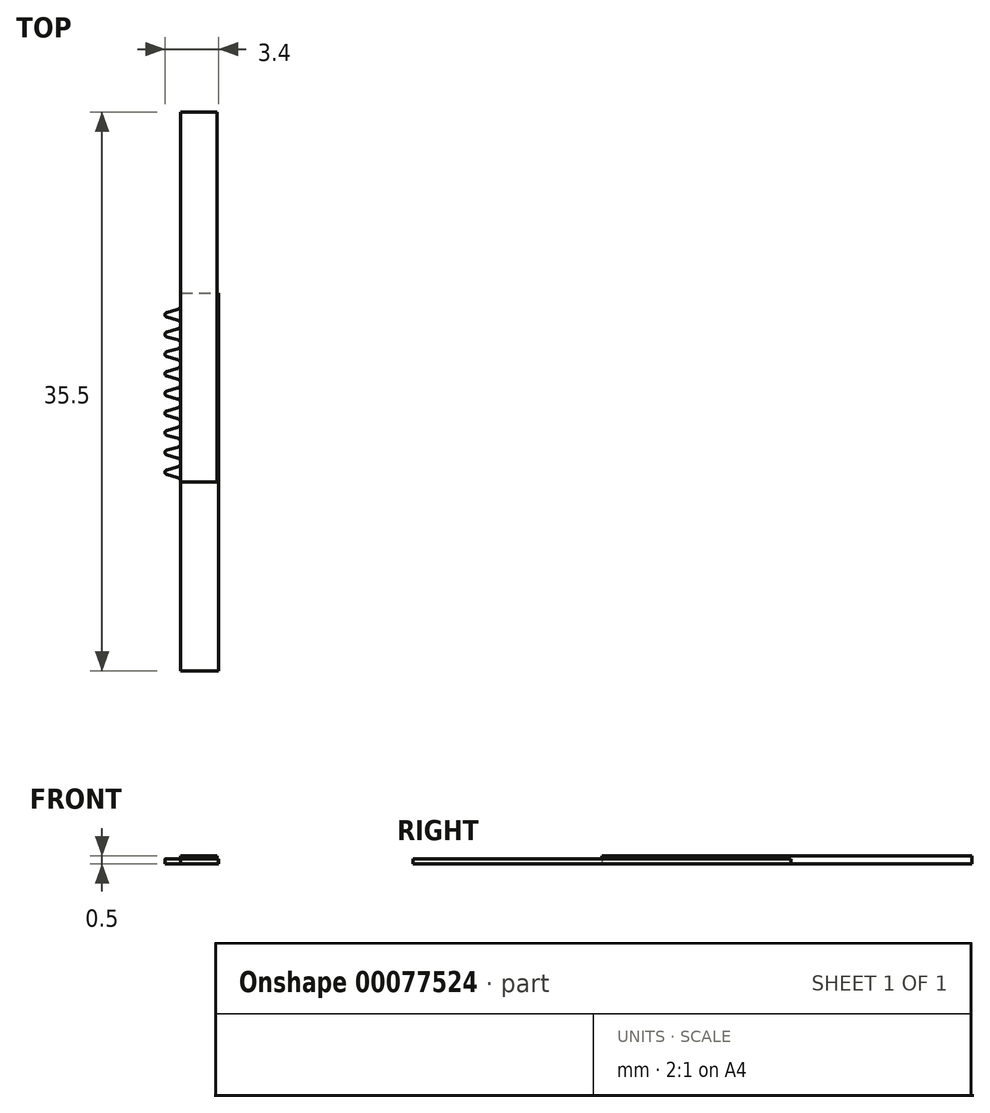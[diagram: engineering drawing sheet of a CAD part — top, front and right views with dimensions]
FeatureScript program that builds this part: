
annotation { "Feature Type Name" : "Feature", "Feature Type Description" : "" }
export const myFeature = defineFeature(function(context is Context, id is Id, definition is map)
    precondition{}
    {
        {
            var Q0;
            Q0=qCreatedBy(makeId("Top.planeOp"),FACE);
            var sketch = newSketch(context, id + "F0", { "sketchPlane" : qUnion([Q0])});
            skLineSegment(sketch, "E0.bottom", {"start": v(0, 12) * mm, "end": v(2.4, 12) * mm});
            skLineSegment(sketch, "E0.top", {"start": v(0, -12) * mm, "end": v(2.4, -12) * mm});
            skLineSegment(sketch, "E0.left", {"start": v(0, 12) * mm, "end": v(0, -12) * mm});
            skLineSegment(sketch, "E0.right", {"start": v(2.4, 12) * mm, "end": v(2.4, -12) * mm});
            skLineSegment(sketch, "E1", {"start": v(2.4, 0.63) * mm, "end": v(-1, 0.62) * mm, "construction": true});
            skLineSegment(sketch, "E2", {"start": v(2.4, 1.88) * mm, "end": v(-1, 1.87) * mm, "construction": true});
            skArc(sketch, "E3", {"start": v(-0.88, 0.78) * mm, "mid": v(-1, 0.62) * mm, "end": v(-0.88, 0.47) * mm});
            skArc(sketch, "E4", {"start": v(-0.22, 0.96) * mm, "mid": v(-0.06, 1.07) * mm, "end": v(0, 1.25) * mm});
            skPoint(sketch, "E5", {"position": v(0, 1.25) * mm});
            skLineSegment(sketch, "E6", {"start": v(-0.88, 0.78) * mm, "end": v(-0.22, 0.96) * mm});
            skArc(sketch, "E7", {"start": v(0, 0) * mm, "mid": v(-0.06, 0.18) * mm, "end": v(-0.22, 0.29) * mm});
            skLineSegment(sketch, "E8", {"start": v(-0.88, 0.47) * mm, "end": v(-0.22, 0.29) * mm});
            skArc(sketch, "E9.1.0.0", {"start": v(-0.22, 2.21) * mm, "mid": v(-0.06, 2.32) * mm, "end": v(0, 2.5) * mm});
            skLineSegment(sketch, "E9.1.0.1", {"start": v(-0.88, 2.03) * mm, "end": v(-0.22, 2.21) * mm});
            skArc(sketch, "E9.1.0.2", {"start": v(-0.88, 2.03) * mm, "mid": v(-1, 1.87) * mm, "end": v(-0.88, 1.72) * mm});
            skLineSegment(sketch, "E9.1.0.3", {"start": v(-0.88, 1.72) * mm, "end": v(-0.22, 1.54) * mm});
            skArc(sketch, "E9.1.0.4", {"start": v(0, 1.25) * mm, "mid": v(-0.06, 1.43) * mm, "end": v(-0.22, 1.54) * mm});
            skArc(sketch, "E9.2.0.0", {"start": v(-0.22, 3.46) * mm, "mid": v(-0.06, 3.57) * mm, "end": v(0, 3.75) * mm});
            skLineSegment(sketch, "E9.2.0.1", {"start": v(-0.88, 3.28) * mm, "end": v(-0.22, 3.46) * mm});
            skArc(sketch, "E9.2.0.2", {"start": v(-0.88, 3.28) * mm, "mid": v(-1, 3.12) * mm, "end": v(-0.88, 2.97) * mm});
            skLineSegment(sketch, "E9.2.0.3", {"start": v(-0.88, 2.97) * mm, "end": v(-0.22, 2.79) * mm});
            skArc(sketch, "E9.2.0.4", {"start": v(0, 2.5) * mm, "mid": v(-0.06, 2.68) * mm, "end": v(-0.22, 2.79) * mm});
            skArc(sketch, "E9.3.0.0", {"start": v(-0.22, 4.71) * mm, "mid": v(-0.06, 4.82) * mm, "end": v(0, 5) * mm});
            skLineSegment(sketch, "E9.3.0.1", {"start": v(-0.88, 4.53) * mm, "end": v(-0.22, 4.71) * mm});
            skArc(sketch, "E9.3.0.2", {"start": v(-0.88, 4.53) * mm, "mid": v(-1, 4.37) * mm, "end": v(-0.88, 4.22) * mm});
            skLineSegment(sketch, "E9.3.0.3", {"start": v(-0.88, 4.22) * mm, "end": v(-0.22, 4.04) * mm});
            skArc(sketch, "E9.3.0.4", {"start": v(0, 3.75) * mm, "mid": v(-0.06, 3.93) * mm, "end": v(-0.22, 4.04) * mm});
            skArc(sketch, "E9.4.0.0", {"start": v(-0.22, 5.96) * mm, "mid": v(-0.06, 6.07) * mm, "end": v(0, 6.25) * mm});
            skLineSegment(sketch, "E9.4.0.1", {"start": v(-0.88, 5.78) * mm, "end": v(-0.22, 5.96) * mm});
            skArc(sketch, "E9.4.0.2", {"start": v(-0.88, 5.78) * mm, "mid": v(-1, 5.62) * mm, "end": v(-0.88, 5.47) * mm});
            skLineSegment(sketch, "E9.4.0.3", {"start": v(-0.88, 5.47) * mm, "end": v(-0.22, 5.29) * mm});
            skArc(sketch, "E9.4.0.4", {"start": v(0, 5) * mm, "mid": v(-0.06, 5.18) * mm, "end": v(-0.22, 5.29) * mm});
            skArc(sketch, "E9.5.0.0", {"start": v(-0.22, 7.21) * mm, "mid": v(-0.06, 7.32) * mm, "end": v(0, 7.5) * mm});
            skLineSegment(sketch, "E9.5.0.1", {"start": v(-0.88, 7.03) * mm, "end": v(-0.22, 7.21) * mm});
            skArc(sketch, "E9.5.0.2", {"start": v(-0.88, 7.03) * mm, "mid": v(-1, 6.88) * mm, "end": v(-0.88, 6.72) * mm});
            skLineSegment(sketch, "E9.5.0.3", {"start": v(-0.88, 6.72) * mm, "end": v(-0.22, 6.54) * mm});
            skArc(sketch, "E9.5.0.4", {"start": v(0, 6.25) * mm, "mid": v(-0.06, 6.43) * mm, "end": v(-0.22, 6.54) * mm});
            skArc(sketch, "E9.6.0.0", {"start": v(-0.22, 8.46) * mm, "mid": v(-0.06, 8.57) * mm, "end": v(0, 8.75) * mm});
            skLineSegment(sketch, "E9.6.0.1", {"start": v(-0.88, 8.28) * mm, "end": v(-0.22, 8.46) * mm});
            skArc(sketch, "E9.6.0.2", {"start": v(-0.88, 8.28) * mm, "mid": v(-1, 8.12) * mm, "end": v(-0.88, 7.97) * mm});
            skLineSegment(sketch, "E9.6.0.3", {"start": v(-0.88, 7.97) * mm, "end": v(-0.22, 7.79) * mm});
            skArc(sketch, "E9.6.0.4", {"start": v(0, 7.5) * mm, "mid": v(-0.06, 7.68) * mm, "end": v(-0.22, 7.79) * mm});
            skArc(sketch, "E9.7.0.0", {"start": v(-0.22, 9.71) * mm, "mid": v(-0.06, 9.82) * mm, "end": v(0, 10) * mm});
            skLineSegment(sketch, "E9.7.0.1", {"start": v(-0.88, 9.53) * mm, "end": v(-0.22, 9.71) * mm});
            skArc(sketch, "E9.7.0.2", {"start": v(-0.88, 9.53) * mm, "mid": v(-1, 9.38) * mm, "end": v(-0.88, 9.22) * mm});
            skLineSegment(sketch, "E9.7.0.3", {"start": v(-0.88, 9.22) * mm, "end": v(-0.22, 9.04) * mm});
            skArc(sketch, "E9.7.0.4", {"start": v(0, 8.75) * mm, "mid": v(-0.06, 8.93) * mm, "end": v(-0.22, 9.04) * mm});
            skArc(sketch, "E9.8.0.0", {"start": v(-0.22, 10.96) * mm, "mid": v(-0.06, 11.07) * mm, "end": v(0, 11.25) * mm});
            skLineSegment(sketch, "E9.8.0.1", {"start": v(-0.88, 10.78) * mm, "end": v(-0.22, 10.96) * mm});
            skArc(sketch, "E9.8.0.2", {"start": v(-0.88, 10.78) * mm, "mid": v(-1, 10.62) * mm, "end": v(-0.88, 10.47) * mm});
            skLineSegment(sketch, "E9.8.0.3", {"start": v(-0.88, 10.47) * mm, "end": v(-0.22, 10.29) * mm});
            skArc(sketch, "E9.8.0.4", {"start": v(0, 10) * mm, "mid": v(-0.06, 10.18) * mm, "end": v(-0.22, 10.29) * mm});
            skLineSegment(sketch, "E9.direction1", {"start": v(-0.22, 0.96) * mm, "end": v(-0.22, 2.21) * mm, "construction": true});
            skSolve(sketch);
        }
        {
            var Q0;
            {var subQ1=sQuery(id+"F0.wireOp",EDGE,"E9.8.0.0");var subQ4=sQuery(id+"F0.wireOp",EDGE,"E9.7.0.0");var subQ8=sQuery(id+"F0.wireOp",EDGE,"E9.6.0.0");var subQ12=sQuery(id+"F0.wireOp",EDGE,"E9.5.0.0");var subQ16=sQuery(id+"F0.wireOp",EDGE,"E9.4.0.0");var subQ20=sQuery(id+"F0.wireOp",EDGE,"E9.3.0.0");var subQ24=sQuery(id+"F0.wireOp",EDGE,"E9.2.0.0");var subQ28=sQuery(id+"F0.wireOp",EDGE,"E9.1.0.0");var subQ39=sQuery(id+"F0.wireOp",EDGE,"E0.bottom");Q0=qUnion([makeQuery(id+"F0.imprint","IMPRINT",FACE,{"disambiguationData":[TD([[makeQuery(id+"F0.imprint","IMPRINT",EDGE,{"derivedFrom":subQ1}),-1.0]])]}),makeQuery(id+"F0.imprint","IMPRINT",FACE,{"disambiguationData":[TD([[makeQuery(id+"F0.imprint","IMPRINT",EDGE,{"derivedFrom":subQ4}),-1.0]])]}),makeQuery(id+"F0.imprint","IMPRINT",FACE,{"disambiguationData":[TD([[makeQuery(id+"F0.imprint","IMPRINT",EDGE,{"derivedFrom":subQ8}),-1.0]])]}),makeQuery(id+"F0.imprint","IMPRINT",FACE,{"disambiguationData":[TD([[makeQuery(id+"F0.imprint","IMPRINT",EDGE,{"derivedFrom":subQ12}),-1.0]])]}),makeQuery(id+"F0.imprint","IMPRINT",FACE,{"disambiguationData":[TD([[makeQuery(id+"F0.imprint","IMPRINT",EDGE,{"derivedFrom":subQ16}),-1.0]])]}),makeQuery(id+"F0.imprint","IMPRINT",FACE,{"disambiguationData":[TD([[makeQuery(id+"F0.imprint","IMPRINT",EDGE,{"derivedFrom":subQ20}),-1.0]])]}),makeQuery(id+"F0.imprint","IMPRINT",FACE,{"disambiguationData":[TD([[makeQuery(id+"F0.imprint","IMPRINT",EDGE,{"derivedFrom":subQ24}),-1.0]])]}),makeQuery(id+"F0.imprint","IMPRINT",FACE,{"disambiguationData":[TD([[makeQuery(id+"F0.imprint","IMPRINT",EDGE,{"derivedFrom":subQ28}),-1.0]])]}),makeQuery(id+"F0.imprint","IMPRINT",FACE,{"disambiguationData":[TD([[makeQuery(id+"F0.imprint","IMPRINT",EDGE,{"derivedFrom":sQuery(id+"F0.wireOp",EDGE,"E3")}),1.0]])]}),makeQuery(id+"F0.imprint","IMPRINT",FACE,{"disambiguationData":[TD([[makeQuery(id+"F0.imprint","IMPRINT",EDGE,{"derivedFrom":subQ39}),-1.0]])]})]);}
            extrude(context, id + "F1", {"entities" : qUnion([Q0]), "depth" : 0.3 * mm});
        }
        {
            var Q0;
            Q0=qCreatedBy(makeId("Top.planeOp"),FACE);
            var sketch = newSketch(context, id + "F2", { "sketchPlane" : qUnion([Q0])});
            skLineSegment(sketch, "E10.bottom", {"start": v(0, 0) * mm, "end": v(2.3, 0) * mm});
            skLineSegment(sketch, "E10.top", {"start": v(0, 23.5) * mm, "end": v(2.3, 23.5) * mm});
            skLineSegment(sketch, "E10.left", {"start": v(0, 0) * mm, "end": v(0, 23.5) * mm});
            skLineSegment(sketch, "E10.right", {"start": v(2.3, 0) * mm, "end": v(2.3, 23.5) * mm});
            skSolve(sketch);
        }
        {
            var Q0;
            Q0=makeQuery(id+"F2.imprint","IMPRINT",FACE,{"disambiguationData":[TD([[makeQuery(id+"F2.imprint","IMPRINT",EDGE,{"derivedFrom":sQuery(id+"F2.wireOp",EDGE,"E10.bottom")}),1.0]])]});
            extrude(context, id + "F3", {"entities" : qUnion([Q0]), "depth" : 0.5 * mm});
        }
    });
